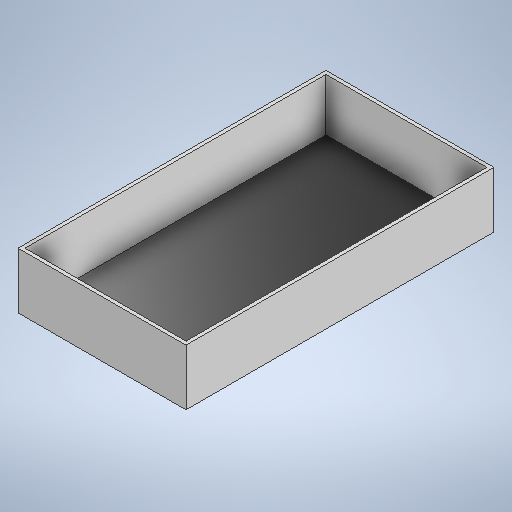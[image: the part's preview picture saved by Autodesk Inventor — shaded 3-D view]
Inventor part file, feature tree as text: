
AUTODESK INVENTOR PART (.ipt)
format: ipt  version: 2025 (Build 290162000, 162)  size: 270,848 bytes
history: native  units: in
note: dims shown in document units (in); Inventor stores cm internally (conversion verified against a paired STEP export)
features: extrude x4, sketch x3
ambient origin geometry x8: Origin, YZ Plane, XZ Plane, XY Plane, X Axis, Y Axis, Z Axis, Center Point
bodies: Solid1 (feature_tree)
feature tree (7):
  sketch  "Sketch1"  dims[d0=22.0in d1=12.0in]
  extrude  "Extrusion1"  Depth=12.0in
  extrude  "Extrusion2"  Depth=11.5in
  extrude  "Extrusion3"  Depth=4.0in TaperAngle=0.0deg
  extrude  "Extrusion5"  Depth=0.7874in
  sketch  "Sketch2"  dims[d2=21.5in d3=11.5in]
  sketch  "Sketch4"  dims[d4=0.25in d5=0.0in d6=4.0in d7=0.0in d8=0.7874in d9=3.937in d10=1.9685in d11=0.0in d17=0.3937in d18=0.3937in d19=0.3937in d20=1.9685in d21=0.0in]
